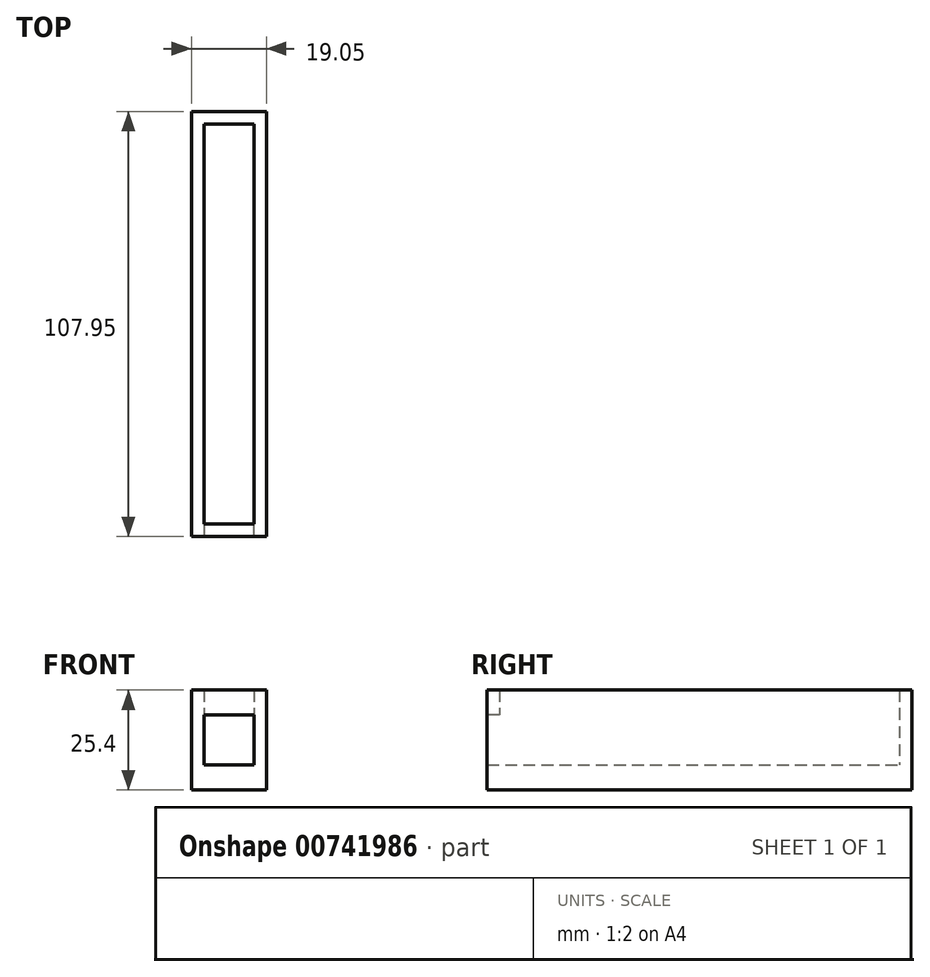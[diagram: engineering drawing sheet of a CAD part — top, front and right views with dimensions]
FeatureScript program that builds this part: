
annotation { "Feature Type Name" : "Feature", "Feature Type Description" : "" }
export const myFeature = defineFeature(function(context is Context, id is Id, definition is map)
    precondition{}
    {
        {
            var Q0;
            Q0=qCreatedBy(makeId("Top.planeOp"),FACE);
            var sketch = newSketch(context, id + "F0", { "sketchPlane" : qUnion([Q0])});
            skLineSegment(sketch, "E0.bottom", {"start": v(-27.52, -68.41) * mm, "end": v(-14.82, -68.41) * mm});
            skLineSegment(sketch, "E0.top", {"start": v(-27.52, 33.19) * mm, "end": v(-14.82, 33.19) * mm});
            skLineSegment(sketch, "E0.left", {"start": v(-27.52, -68.41) * mm, "end": v(-27.52, 33.19) * mm});
            skLineSegment(sketch, "E0.right", {"start": v(-14.82, -68.41) * mm, "end": v(-14.82, 33.19) * mm});
            skLineSegment(sketch, "E1.bottom", {"start": v(-30.7, 36.36) * mm, "end": v(-11.65, 36.36) * mm});
            skLineSegment(sketch, "E1.top", {"start": v(-30.7, -71.59) * mm, "end": v(-11.65, -71.59) * mm});
            skLineSegment(sketch, "E1.left", {"start": v(-30.7, 36.36) * mm, "end": v(-30.7, -71.59) * mm});
            skLineSegment(sketch, "E1.right", {"start": v(-11.65, 36.36) * mm, "end": v(-11.65, -71.59) * mm});
            skSolve(sketch);
        }
        {
            var Q0;
            Q0=makeQuery(id+"F0.imprint","IMPRINT",FACE,{"disambiguationData":[TD([[makeQuery(id+"F0.imprint","IMPRINT",EDGE,{"derivedFrom":sQuery(id+"F0.wireOp",EDGE,"E0.bottom")}),-1.0]])]});
            extrude(context, id + "F1", {"entities" : qUnion([Q0]), "depth" : 25.4 * mm, "offsetDistance" : 25.4 * mm});
        }
        {
            var Q0;
            Q0=makeQuery(id+"F0.imprint","IMPRINT",FACE,{"disambiguationData":[TD([[makeQuery(id+"F0.imprint","IMPRINT",EDGE,{"derivedFrom":sQuery(id+"F0.wireOp",EDGE,"E0.bottom")}),1.0]])]});
            extrude(context, id + "F2", {"entities" : qUnion([Q0]), "operationType" : NewBodyOperationType.ADD, "depth" : 6.35 * mm, "offsetDistance" : 25.4 * mm});
        }
        {
            var Q0;
            Q0=makeQuery(id+"F1.opExtrude","SWEPT_FACE",FACE,{"disambiguationData":[OSD([sQuery(id+"F0.wireOp",EDGE,"E1.top")])]});
            var sketch = newSketch(context, id + "F3", { "sketchPlane" : qUnion([Q0])});
            skLineSegment(sketch, "E2", {"start": v(-30.7, 25.4) * mm, "end": v(-30.7, 0) * mm});
            skLineSegment(sketch, "E3", {"start": v(-30.7, 0) * mm, "end": v(-30.7, 6.35) * mm});
            skLineSegment(sketch, "E4", {"start": v(-30.7, 0) * mm, "end": v(-27.52, 0) * mm});
            skLineSegment(sketch, "E5.bottom", {"start": v(-27.52, 6.35) * mm, "end": v(-14.82, 6.35) * mm});
            skLineSegment(sketch, "E5.top", {"start": v(-27.52, 19.05) * mm, "end": v(-14.82, 19.05) * mm});
            skLineSegment(sketch, "E5.left", {"start": v(-27.52, 6.35) * mm, "end": v(-27.52, 19.05) * mm});
            skLineSegment(sketch, "E5.right", {"start": v(-14.82, 6.35) * mm, "end": v(-14.82, 19.05) * mm});
            skSolve(sketch);
        }
        {
            var Q0;
            Q0=makeQuery(id+"F3.imprint","IMPRINT",FACE,{"disambiguationData":[TD([[makeQuery(id+"F3.imprint","IMPRINT",EDGE,{"derivedFrom":sQuery(id+"F3.wireOp",EDGE,"E5.bottom")}),1.0]])]});
            extrude(context, id + "F4", {"entities" : qUnion([Q0]), "operationType" : NewBodyOperationType.REMOVE, "oppositeDirection" : true, "depth" : 25.4 * mm, "offsetDistance" : 25.4 * mm});
        }
    });
